# Revit family: Haworth_Compose_Worksurface_Bent
name_source: partatom
category: Furniture Systems
revit_build: Autodesk Revit 2018 (Build: 20170223_1515(x64)
units: mm (PartAtom-declared; Revit-internal decimal feet)

## family parameters
Always vertical = Yes
Cut with Voids When Loaded = No
OmniClass Number = 23.40.70.14.64.21
OmniClass Title = Systems Furniture
Part Type = Normal
Room Calculation Point = No
Round Connector Dimension = Use Diameter
Shared = No
Work Plane-Based = No

## types (8) — shared parameters
Actual Depth Left = 30"
Actual Depth Right = 24"
Actual Height = 29"
Assembly Code = E2020200
Cantilever Bracket = Yes
Cantilever Bracket Location = 1 3/4"
Custom Size = No
Description = Haworth - Worksurface - Compose Bent
Disc Base Support = No
Double Support Leg = No
End Support Location = 1 3/4"
Height = 29"
Manufacturer = Haworth
Max. Height = 48"
Max. Length = 60"
Max. Width = 30"
Min. Height = 26"
Min. Length = 24"
Min. Width = 24"
Min/Max Width = 36-60 in.
Model = WUCB
Revision Number = 3
Size = Verify Final Dim. w/ Haworth
Standard Depth = 24, 30 in.
Support Column = No
Support Finish = Haworth _ Paint _ Metallic Champagne
Support Height = 27 13/16"
Support Panel = No
Support Post_45 Degree = No
Support Post_90 Degree = No
Sustainability Info = http://media.haworth.com
Top Thickness = 1 3/16"
URL = www.haworth.com
URL - Product = http://www.haworth.com
Warranty = http://www.haworth.com
Worksurface Edge Finish = Haworth _ Laminate _ Maple H-AE
Worksurface Finish = Haworth _ Laminate _ Maple H-AE

## per-type parameters (varying)
| type | Actual Length | Actual Width | Length | Short Bend Width |
| 60w 30d | 60" | 30" | 60" | No |
| 48w 30d | 48" | 30" | 48" | No |
| 42w 30d | 42" | 30" | 42" | No |
| 36w 30d | 36" | 30" | 36" | No |
| 60w 24d | 60" | 24" | 60" | Yes |
| 48w 24d | 48" | 24" | 48" | Yes |
| 42w 24d | 42" | 24" | 42" | Yes |
| 36w 24d | 36" | 24" | 36" | Yes |

## geometry (parser evidence)
native form markers: Sweep x10
no freeform markers — native parametric forms only
